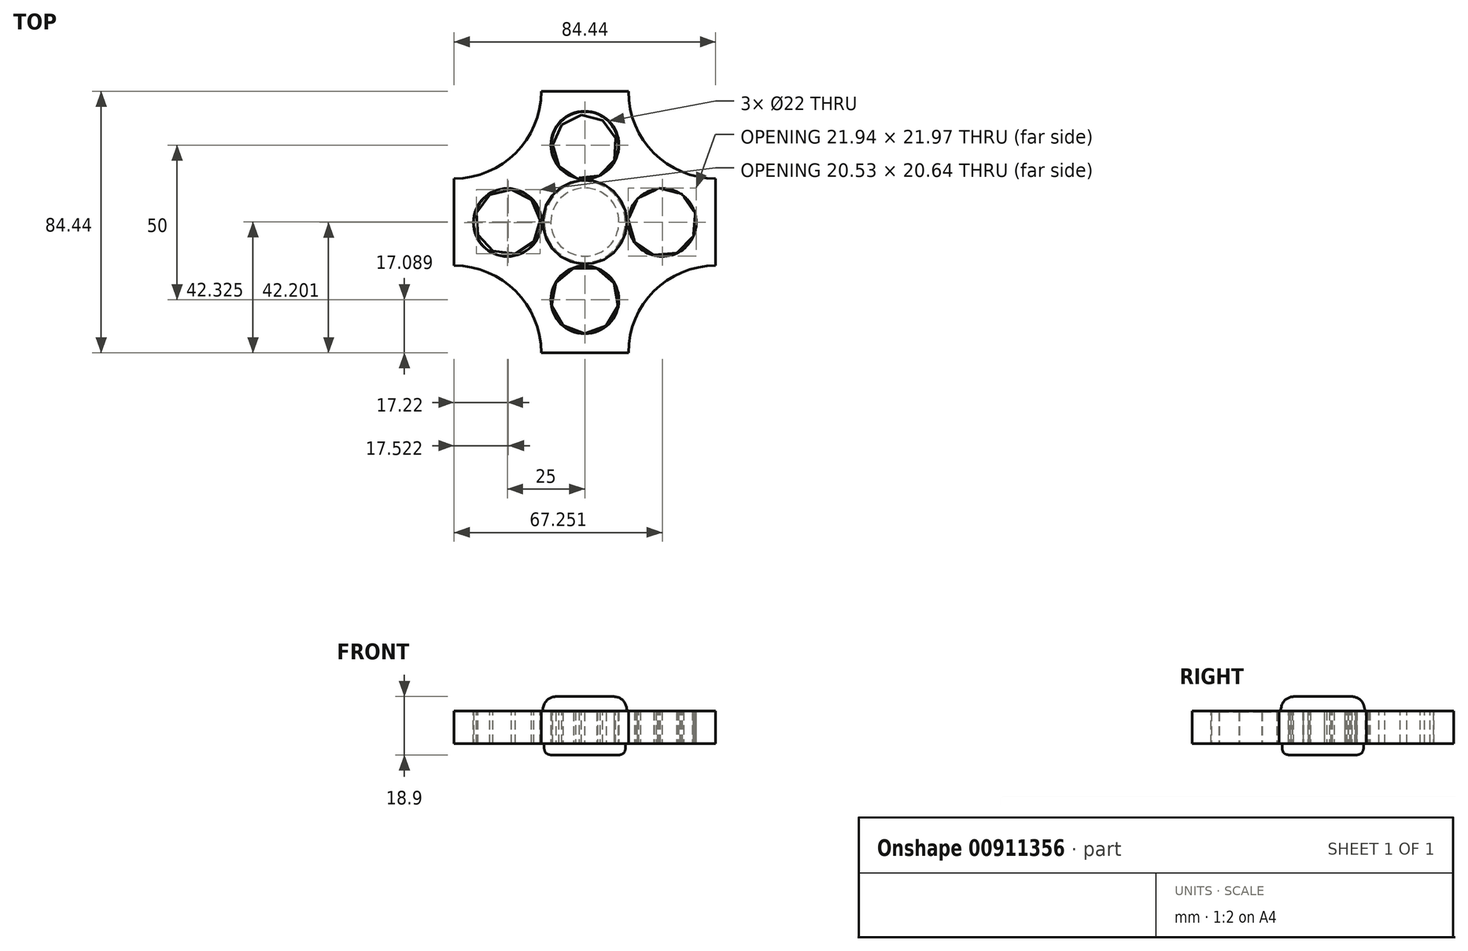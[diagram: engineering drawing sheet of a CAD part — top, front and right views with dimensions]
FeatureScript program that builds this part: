
annotation { "Feature Type Name" : "Feature", "Feature Type Description" : "" }
export const myFeature = defineFeature(function(context is Context, id is Id, definition is map)
    precondition{}
    {
        {
            var Q0;
            Q0=qCreatedBy(makeId("Top.planeOp"),FACE);
            var sketch = newSketch(context, id + "F0", { "sketchPlane" : qUnion([Q0])});
            skCircle(sketch, "E0", {"center": v(0, 0) * mm, "radius": 11 * mm});
            skSolve(sketch);
        }
        {
            var Q0;
            Q0=qCreatedBy(makeId("Top.planeOp"),FACE);
            var sketch = newSketch(context, id + "F1", { "sketchPlane" : qUnion([Q0])});
            skLineSegment(sketch, "E1.bottom", {"start": v(0, 0) * mm, "end": v(-14.07, 0) * mm});
            skLineSegment(sketch, "E1.top", {"start": v(0, 42.22) * mm, "end": v(-14.07, 42.22) * mm});
            skLineSegment(sketch, "E1.left", {"start": v(0, 0) * mm, "end": v(0, 42.22) * mm});
            skLineSegment(sketch, "E1.right", {"start": v(-14.07, 0) * mm, "end": v(-14.07, 42.22) * mm});
            skLineSegment(sketch, "E2.bottom", {"start": v(0, 0) * mm, "end": v(14.07, 0) * mm});
            skLineSegment(sketch, "E2.top", {"start": v(0, 42.22) * mm, "end": v(14.07, 42.22) * mm});
            skLineSegment(sketch, "E2.right", {"start": v(14.07, 0) * mm, "end": v(14.07, 42.22) * mm});
            skLineSegment(sketch, "E3.bottom", {"start": v(0, 0) * mm, "end": v(42.22, 0) * mm});
            skLineSegment(sketch, "E3.top", {"start": v(0, 14.07) * mm, "end": v(42.22, 14.07) * mm});
            skLineSegment(sketch, "E3.left", {"start": v(0, 0) * mm, "end": v(0, 14.07) * mm});
            skLineSegment(sketch, "E3.right", {"start": v(42.22, 0) * mm, "end": v(42.22, 14.07) * mm});
            skLineSegment(sketch, "E4.top", {"start": v(0, -14.07) * mm, "end": v(42.22, -14.07) * mm});
            skLineSegment(sketch, "E4.left", {"start": v(0, 0) * mm, "end": v(0, -14.07) * mm});
            skLineSegment(sketch, "E4.right", {"start": v(42.22, 0) * mm, "end": v(42.22, -14.07) * mm});
            skLineSegment(sketch, "E5.top", {"start": v(0, -42.22) * mm, "end": v(14.07, -42.22) * mm});
            skLineSegment(sketch, "E5.left", {"start": v(0, 0) * mm, "end": v(0, -42.22) * mm});
            skLineSegment(sketch, "E5.right", {"start": v(14.07, 0) * mm, "end": v(14.07, -42.22) * mm});
            skLineSegment(sketch, "E6.top", {"start": v(0, -42.22) * mm, "end": v(-14.07, -42.22) * mm});
            skLineSegment(sketch, "E6.right", {"start": v(-14.07, 0) * mm, "end": v(-14.07, -42.22) * mm});
            skLineSegment(sketch, "E7.bottom", {"start": v(0, 0) * mm, "end": v(-42.22, 0) * mm});
            skLineSegment(sketch, "E7.top", {"start": v(0, -14.07) * mm, "end": v(-42.22, -14.07) * mm});
            skLineSegment(sketch, "E7.right", {"start": v(-42.22, 0) * mm, "end": v(-42.22, -14.07) * mm});
            skLineSegment(sketch, "E8.top", {"start": v(0, 14.07) * mm, "end": v(-42.22, 14.07) * mm});
            skLineSegment(sketch, "E8.right", {"start": v(-42.22, 0) * mm, "end": v(-42.22, 14.07) * mm});
            skArc(sketch, "E9", {"start": v(-42.22, 14.07) * mm, "mid": v(-22.32, 22.32) * mm, "end": v(-14.07, 42.22) * mm});
            skArc(sketch, "E10", {"start": v(-14.07, -42.22) * mm, "mid": v(-22.32, -22.32) * mm, "end": v(-42.22, -14.07) * mm});
            skArc(sketch, "E11", {"start": v(42.22, -14.07) * mm, "mid": v(22.32, -22.32) * mm, "end": v(14.07, -42.22) * mm});
            skArc(sketch, "E12", {"start": v(14.07, 42.22) * mm, "mid": v(22.32, 22.32) * mm, "end": v(42.22, 14.07) * mm});
            skLineSegment(sketch, "E13", {"start": v(0, -14.07) * mm, "end": v(0, -15.37) * mm});
            skSolve(sketch);
        }
        {
            var Q0;
            Q0=makeQuery(id+"F0.imprint","IMPRINT",FACE,{"disambiguationData":[TD([[makeQuery(id+"F0.imprint","IMPRINT",EDGE,{"derivedFrom":sQuery(id+"F0.wireOp",EDGE,"E0")}),1.0]])]});
            var Q1;
            {var subQ0=sQuery(id+"F1.wireOp",EDGE,"E3.bottom");Q1=makeQuery(id+"F1.imprint","IMPRINT",FACE,{"disambiguationData":[TD([[makeQuery(id+"F1.imprint","IMPRINT",EDGE,{"derivedFrom":subQ0}),1.0]])]});}
            var Q2;
            {var subQ1=sQuery(id+"F1.wireOp",EDGE,"E5.top");Q2=makeQuery(id+"F1.imprint","IMPRINT",FACE,{"disambiguationData":[TD([[makeQuery(id+"F1.imprint","IMPRINT",EDGE,{"derivedFrom":subQ1}),1.0]])]});}
            var Q3;
            {var subQ0=sQuery(id+"F1.wireOp",EDGE,"E7.bottom");Q3=makeQuery(id+"F1.imprint","IMPRINT",FACE,{"disambiguationData":[TD([[makeQuery(id+"F1.imprint","IMPRINT",EDGE,{"derivedFrom":subQ0}),-1.0]])]});}
            var Q4;
            {var subQ0=sQuery(id+"F1.wireOp",EDGE,"E1.bottom");Q4=makeQuery(id+"F1.imprint","IMPRINT",FACE,{"disambiguationData":[TD([[makeQuery(id+"F1.imprint","IMPRINT",EDGE,{"derivedFrom":subQ0}),1.0]])]});}
            var Q5;
            {var subQ0=sQuery(id+"F1.wireOp",EDGE,"E12");Q5=makeQuery(id+"F1.imprint","IMPRINT",FACE,{"disambiguationData":[TD([[makeQuery(id+"F1.imprint","IMPRINT",EDGE,{"derivedFrom":subQ0}),-1.0]])]});}
            var Q6;
            {var subQ0=sQuery(id+"F1.wireOp",EDGE,"E1.top");Q6=makeQuery(id+"F1.imprint","IMPRINT",FACE,{"disambiguationData":[TD([[makeQuery(id+"F1.imprint","IMPRINT",EDGE,{"derivedFrom":subQ0}),1.0]])]});}
            var Q7;
            {var subQ0=sQuery(id+"F1.wireOp",EDGE,"E6.top");Q7=makeQuery(id+"F1.imprint","IMPRINT",FACE,{"disambiguationData":[TD([[makeQuery(id+"F1.imprint","IMPRINT",EDGE,{"derivedFrom":subQ0}),-1.0]])]});}
            var Q8;
            {var subQ0=sQuery(id+"F1.wireOp",EDGE,"E10");Q8=makeQuery(id+"F1.imprint","IMPRINT",FACE,{"disambiguationData":[TD([[makeQuery(id+"F1.imprint","IMPRINT",EDGE,{"derivedFrom":subQ0}),-1.0]])]});}
            var Q9;
            {var subQ0=sQuery(id+"F1.wireOp",EDGE,"E1.bottom");Q9=makeQuery(id+"F1.imprint","IMPRINT",FACE,{"disambiguationData":[TD([[makeQuery(id+"F1.imprint","IMPRINT",EDGE,{"derivedFrom":subQ0}),-1.0]])]});}
            var Q10;
            {var subQ0=sQuery(id+"F1.wireOp",EDGE,"E9");Q10=makeQuery(id+"F1.imprint","IMPRINT",FACE,{"disambiguationData":[TD([[makeQuery(id+"F1.imprint","IMPRINT",EDGE,{"derivedFrom":subQ0}),-1.0]])]});}
            var Q11;
            {var subQ3=sQuery(id+"F1.wireOp",EDGE,"E11");Q11=makeQuery(id+"F1.imprint","IMPRINT",FACE,{"disambiguationData":[TD([[makeQuery(id+"F1.imprint","IMPRINT",EDGE,{"derivedFrom":subQ3}),-1.0]])]});}
            var Q12;
            {var subQ0=sQuery(id+"F1.wireOp",EDGE,"E3.bottom");Q12=makeQuery(id+"F1.imprint","IMPRINT",FACE,{"disambiguationData":[TD([[makeQuery(id+"F1.imprint","IMPRINT",EDGE,{"derivedFrom":subQ0}),-1.0]])]});}
            var Q13;
            {var subQ0=sQuery(id+"F1.wireOp",EDGE,"E2.bottom");Q13=makeQuery(id+"F1.imprint","IMPRINT",FACE,{"disambiguationData":[TD([[makeQuery(id+"F1.imprint","IMPRINT",EDGE,{"derivedFrom":subQ0}),1.0]])]});}
            var Q14;
            {var subQ0=sQuery(id+"F1.wireOp",EDGE,"E2.top");Q14=makeQuery(id+"F1.imprint","IMPRINT",FACE,{"disambiguationData":[TD([[makeQuery(id+"F1.imprint","IMPRINT",EDGE,{"derivedFrom":subQ0}),-1.0]])]});}
            var Q15;
            {var subQ0=sQuery(id+"F1.wireOp",EDGE,"E7.bottom");Q15=makeQuery(id+"F1.imprint","IMPRINT",FACE,{"disambiguationData":[TD([[makeQuery(id+"F1.imprint","IMPRINT",EDGE,{"derivedFrom":subQ0}),1.0]])]});}
            var Q16;
            {var subQ0=sQuery(id+"F1.wireOp",EDGE,"E2.bottom");Q16=makeQuery(id+"F1.imprint","IMPRINT",FACE,{"disambiguationData":[TD([[makeQuery(id+"F1.imprint","IMPRINT",EDGE,{"derivedFrom":subQ0}),-1.0]])]});}
            extrude(context, id + "F2", {"entities" : qUnion([Q0, Q1, Q2, Q3, Q4, Q5, Q6, Q7, Q8, Q9, Q10, Q11, Q12, Q13, Q14, Q15, Q16]), "depth" : 10.6 * mm, "offsetDistance" : 25 * mm});
        }
        {
            var Q0;
            Q0=makeQuery(id+"F2.opExtrude","CAP_FACE",FACE,{"disambiguationData":[OSD([sQuery(id+"F1.wireOp",EDGE,"E1.top"),sQuery(id+"F1.wireOp",EDGE,"E2.top"),sQuery(id+"F1.wireOp",EDGE,"E3.right"),sQuery(id+"F1.wireOp",EDGE,"E4.right"),sQuery(id+"F1.wireOp",EDGE,"E5.top"),sQuery(id+"F1.wireOp",EDGE,"E6.top"),sQuery(id+"F1.wireOp",EDGE,"E7.right"),sQuery(id+"F1.wireOp",EDGE,"E8.right"),sQuery(id+"F1.wireOp",EDGE,"E9"),sQuery(id+"F1.wireOp",EDGE,"E10"),sQuery(id+"F1.wireOp",EDGE,"E11"),sQuery(id+"F1.wireOp",EDGE,"E12")])],"isStart":false});
            var sketch = newSketch(context, id + "F3", { "sketchPlane" : qUnion([Q0])});
            skCircle(sketch, "E14", {"center": v(0, 0) * mm, "radius": 11.22 * mm});
            skSolve(sketch);
        }
        {
            var Q0;
            Q0=makeQuery(id+"F3.imprint","IMPRINT",FACE,{"disambiguationData":[TD([[makeQuery(id+"F3.imprint","IMPRINT",EDGE,{"derivedFrom":sQuery(id+"F3.wireOp",EDGE,"E14")}),-1.0]])]});
            var sketch = newSketch(context, id + "F4", { "sketchPlane" : qUnion([Q0])});
            skLineSegment(sketch, "E15", {"start": v(0, 0) * mm, "end": v(0, 24.87) * mm});
            skCircle(sketch, "E16", {"center": v(25, -0.13) * mm, "radius": 11 * mm});
            skCircle(sketch, "E17", {"center": v(0, 24.87) * mm, "radius": 11 * mm});
            skCircle(sketch, "E18", {"center": v(-25, -0.13) * mm, "radius": 11 * mm});
            skCircle(sketch, "E19", {"center": v(0, -25.13) * mm, "radius": 11 * mm});
            skSolve(sketch);
        }
        {
            var Q0;
            Q0 = qSketchRegion(id + "F4", true);
            extrude(context, id + "F5", {"entities" : qUnion([Q0]), "operationType" : NewBodyOperationType.REMOVE, "oppositeDirection" : true, "depth" : 25 * mm, "offsetDistance" : 25 * mm});
        }
        {
            var Q0;
            Q0=makeQuery(id+"F2.opExtrude","CAP_FACE",FACE,{"disambiguationData":[OSD([sQuery(id+"F0.wireOp",EDGE,"E0")])],"isStart":true});
            var sketch = newSketch(context, id + "F6", { "sketchPlane" : qUnion([Q0])});
            skCircle(sketch, "E20", {"center": v(0, 0) * mm, "radius": 13.13 * mm});
            skSolve(sketch);
        }
        {
            var Q0;
            Q0 = qSketchRegion(id + "F6", true);
            extrude(context, id + "F7", {"entities" : qUnion([Q0]), "depth" : 3.6 * mm, "offsetDistance" : 25 * mm});
        }
        {
            var Q0;
            Q0=makeQuery(id+"F7.opExtrude","CAP_FACE",FACE,{"disambiguationData":[OSD([sQuery(id+"F6.wireOp",EDGE,"E20")])],"isStart":false});
            fillet(context, id + "F8", {"entities" : qUnion([Q0]), "radius" : 2.41 * mm, "tangentPropagation" : true, "rho" : 0.5, "crossSection" : FilletCrossSection.CONIC, "allowEdgeOverflow" : false});
        }
        {
            var Q0;
            Q0=makeQuery(id+"F3.imprint","IMPRINT",FACE,{"disambiguationData":[TD([[makeQuery(id+"F3.imprint","IMPRINT",EDGE,{"derivedFrom":sQuery(id+"F3.wireOp",EDGE,"E14")}),1.0]])]});
            var sketch = newSketch(context, id + "F9", { "sketchPlane" : qUnion([Q0])});
            skCircle(sketch, "E21", {"center": v(0, 0) * mm, "radius": 13.6 * mm});
            skSolve(sketch);
        }
        {
            var Q0;
            Q0 = qSketchRegion(id + "F9", true);
            extrude(context, id + "F10", {"entities" : qUnion([Q0]), "depth" : 4.7 * mm, "offsetDistance" : 25 * mm});
        }
        {
            var Q0;
            Q0=makeQuery(id+"F10.opExtrude","CAP_EDGE",EDGE,{"disambiguationData":[OSD([sQuery(id+"F9.wireOp",EDGE,"E21")])],"isStart":false});
            fillet(context, id + "F11", {"entities" : qUnion([Q0]), "radius" : 5 * mm, "tangentPropagation" : true, "rho" : 0.5, "crossSection" : FilletCrossSection.CONIC, "allowEdgeOverflow" : false});
        }
        {
            var Q0;
            Q0=makeQuery(id+"F2.opExtrude","CAP_FACE",FACE,{"disambiguationData":[OSD([sQuery(id+"F1.wireOp",EDGE,"E1.top"),sQuery(id+"F1.wireOp",EDGE,"E2.top"),sQuery(id+"F1.wireOp",EDGE,"E3.right"),sQuery(id+"F1.wireOp",EDGE,"E4.right"),sQuery(id+"F1.wireOp",EDGE,"E5.top"),sQuery(id+"F1.wireOp",EDGE,"E6.top"),sQuery(id+"F1.wireOp",EDGE,"E7.right"),sQuery(id+"F1.wireOp",EDGE,"E8.right"),sQuery(id+"F1.wireOp",EDGE,"E9"),sQuery(id+"F1.wireOp",EDGE,"E10"),sQuery(id+"F1.wireOp",EDGE,"E11"),sQuery(id+"F1.wireOp",EDGE,"E12")])],"isStart":true});
            var sketch = newSketch(context, id + "F12", { "sketchPlane" : qUnion([Q0])});
            skCircle(sketch, "E22", {"center": v(0, 25.13) * mm, "radius": 10.88 * mm});
            skSolve(sketch);
        }
        {
            var Q0;
            Q0 = qSketchRegion(id + "F12", true);
            extrude(context, id + "F13", {"entities" : qUnion([Q0]), "oppositeDirection" : true, "depth" : 10.3 * mm, "offsetDistance" : 25 * mm});
        }
        {
            var Q0;
            Q0=makeQuery(id+"F13.opExtrude","CAP_FACE",FACE,{"disambiguationData":[OSD([sQuery(id+"F12.wireOp",EDGE,"E22")])],"isStart":true});
            var sketch = newSketch(context, id + "F14", { "sketchPlane" : qUnion([Q0])});
            skCircle(sketch, "E23.cCircle", {"center": v(0, 25.13) * mm, "radius": 10.88 * mm, "construction": true});
            skLineSegment(sketch, "E23.0", {"start": v(9.47, 19.78) * mm, "end": v(3.8, 14.94) * mm});
            skLineSegment(sketch, "E23.1", {"start": v(3.8, 14.94) * mm, "end": v(-3.63, 14.88) * mm});
            skLineSegment(sketch, "E23.2", {"start": v(-3.63, 14.88) * mm, "end": v(-9.37, 19.61) * mm});
            skLineSegment(sketch, "E23.3", {"start": v(-9.37, 19.61) * mm, "end": v(-10.73, 26.93) * mm});
            skLineSegment(sketch, "E23.4", {"start": v(-10.73, 26.93) * mm, "end": v(-7.06, 33.4) * mm});
            skLineSegment(sketch, "E23.5", {"start": v(-7.06, 33.4) * mm, "end": v(-0.1, 36) * mm});
            skLineSegment(sketch, "E23.6", {"start": v(-0.1, 36) * mm, "end": v(6.92, 33.52) * mm});
            skLineSegment(sketch, "E23.7", {"start": v(6.92, 33.52) * mm, "end": v(10.7, 27.11) * mm});
            skLineSegment(sketch, "E23.8", {"start": v(10.7, 27.11) * mm, "end": v(9.47, 19.78) * mm});
            skSolve(sketch);
        }
        {
            var Q0;
            Q0 = qSketchRegion(id + "F14", true);
            extrude(context, id + "F15", {"entities" : qUnion([Q0]), "operationType" : NewBodyOperationType.REMOVE, "oppositeDirection" : true, "depth" : 25 * mm, "offsetDistance" : 25 * mm});
        }
        {
            var Q0;
            Q0=makeQuery(id+"F2.opExtrude","CAP_FACE",FACE,{"disambiguationData":[OSD([sQuery(id+"F1.wireOp",EDGE,"E1.top"),sQuery(id+"F1.wireOp",EDGE,"E2.top"),sQuery(id+"F1.wireOp",EDGE,"E3.right"),sQuery(id+"F1.wireOp",EDGE,"E4.right"),sQuery(id+"F1.wireOp",EDGE,"E5.top"),sQuery(id+"F1.wireOp",EDGE,"E6.top"),sQuery(id+"F1.wireOp",EDGE,"E7.right"),sQuery(id+"F1.wireOp",EDGE,"E8.right"),sQuery(id+"F1.wireOp",EDGE,"E9"),sQuery(id+"F1.wireOp",EDGE,"E10"),sQuery(id+"F1.wireOp",EDGE,"E11"),sQuery(id+"F1.wireOp",EDGE,"E12")])],"isStart":true});
            var sketch = newSketch(context, id + "F16", { "sketchPlane" : qUnion([Q0])});
            skCircle(sketch, "E24", {"center": v(25, 0.13) * mm, "radius": 10.84 * mm});
            skCircle(sketch, "E25", {"center": v(0, -24.87) * mm, "radius": 10.8 * mm});
            skCircle(sketch, "E26", {"center": v(-25, 0.13) * mm, "radius": 10.92 * mm});
            skSolve(sketch);
        }
        {
            var Q0;
            Q0 = qSketchRegion(id + "F16", true);
            extrude(context, id + "F17", {"entities" : qUnion([Q0]), "oppositeDirection" : true, "depth" : 10.6 * mm, "offsetDistance" : 25 * mm});
        }
        {
            var Q0;
            Q0=makeQuery(id+"F3.imprint","IMPRINT",FACE,{"disambiguationData":[TD([[makeQuery(id+"F3.imprint","IMPRINT",EDGE,{"derivedFrom":sQuery(id+"F3.wireOp",EDGE,"E14")}),-1.0]])]});
            var sketch = newSketch(context, id + "F18", { "sketchPlane" : qUnion([Q0])});
            skCircle(sketch, "E27.cCircle", {"center": v(-24.91, 0) * mm, "radius": 10.5 * mm, "construction": true});
            skLineSegment(sketch, "E27.0", {"start": v(-16.5, -6.28) * mm, "end": v(-22.5, -10.22) * mm});
            skLineSegment(sketch, "E27.1", {"start": v(-22.5, -10.22) * mm, "end": v(-29.63, -9.38) * mm});
            skLineSegment(sketch, "E27.2", {"start": v(-29.63, -9.38) * mm, "end": v(-34.55, -4.15) * mm});
            skLineSegment(sketch, "E27.3", {"start": v(-34.55, -4.15) * mm, "end": v(-34.96, 3.02) * mm});
            skLineSegment(sketch, "E27.4", {"start": v(-34.96, 3.02) * mm, "end": v(-30.67, 8.78) * mm});
            skLineSegment(sketch, "E27.5", {"start": v(-30.67, 8.78) * mm, "end": v(-23.68, 10.43) * mm});
            skLineSegment(sketch, "E27.6", {"start": v(-23.68, 10.43) * mm, "end": v(-17.27, 7.2) * mm});
            skLineSegment(sketch, "E27.7", {"start": v(-17.27, 7.2) * mm, "end": v(-14.43, 0.6) * mm});
            skLineSegment(sketch, "E27.8", {"start": v(-14.43, 0.6) * mm, "end": v(-16.5, -6.28) * mm});
            skCircle(sketch, "E28.cCircle", {"center": v(0, 24.26) * mm, "radius": 10.4 * mm, "construction": true});
            skLineSegment(sketch, "E28.0", {"start": v(9.5, 20.05) * mm, "end": v(4.58, 14.92) * mm});
            skLineSegment(sketch, "E28.1", {"start": v(4.58, 14.92) * mm, "end": v(-2.5, 14.17) * mm});
            skLineSegment(sketch, "E28.2", {"start": v(-2.5, 14.17) * mm, "end": v(-8.4, 18.13) * mm});
            skLineSegment(sketch, "E28.3", {"start": v(-8.4, 18.13) * mm, "end": v(-10.37, 24.96) * mm});
            skLineSegment(sketch, "E28.4", {"start": v(-10.37, 24.96) * mm, "end": v(-7.5, 31.46) * mm});
            skLineSegment(sketch, "E28.5", {"start": v(-7.5, 31.46) * mm, "end": v(-1.1, 34.6) * mm});
            skLineSegment(sketch, "E28.6", {"start": v(-1.1, 34.6) * mm, "end": v(5.8, 32.89) * mm});
            skLineSegment(sketch, "E28.7", {"start": v(5.8, 32.89) * mm, "end": v(9.99, 27.15) * mm});
            skLineSegment(sketch, "E28.8", {"start": v(9.99, 27.15) * mm, "end": v(9.5, 20.05) * mm});
            skCircle(sketch, "E29.cCircle", {"center": v(25.04, 0) * mm, "radius": 11.02 * mm, "construction": true});
            skLineSegment(sketch, "E29.0", {"start": v(35.08, -4.55) * mm, "end": v(29.8, -9.93) * mm});
            skLineSegment(sketch, "E29.1", {"start": v(29.8, -9.93) * mm, "end": v(22.3, -10.67) * mm});
            skLineSegment(sketch, "E29.2", {"start": v(22.3, -10.67) * mm, "end": v(16.09, -6.42) * mm});
            skLineSegment(sketch, "E29.3", {"start": v(16.09, -6.42) * mm, "end": v(14.06, 0.84) * mm});
            skLineSegment(sketch, "E29.4", {"start": v(14.06, 0.84) * mm, "end": v(17.17, 7.7) * mm});
            skLineSegment(sketch, "E29.5", {"start": v(17.17, 7.7) * mm, "end": v(23.97, 10.96) * mm});
            skLineSegment(sketch, "E29.6", {"start": v(23.97, 10.96) * mm, "end": v(31.27, 9.1) * mm});
            skLineSegment(sketch, "E29.7", {"start": v(31.27, 9.1) * mm, "end": v(35.65, 2.97) * mm});
            skLineSegment(sketch, "E29.8", {"start": v(35.65, 2.97) * mm, "end": v(35.08, -4.55) * mm});
            skSolve(sketch);
        }
        {
            var Q0;
            Q0 = qSketchRegion(id + "F18", true);
            extrude(context, id + "F19", {"entities" : qUnion([Q0]), "operationType" : NewBodyOperationType.REMOVE, "oppositeDirection" : true, "depth" : 25 * mm, "offsetDistance" : 25 * mm});
        }
    });
